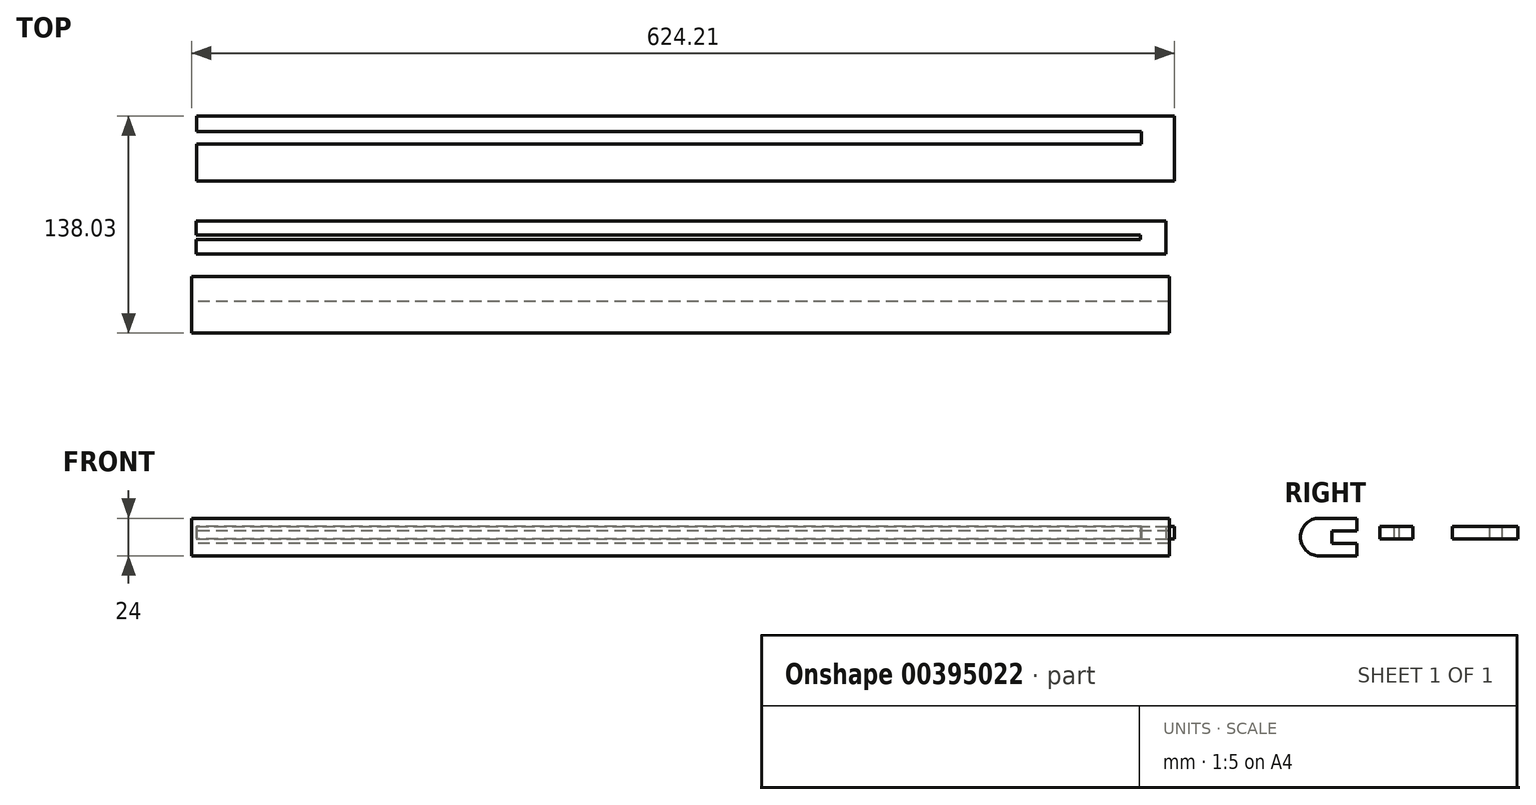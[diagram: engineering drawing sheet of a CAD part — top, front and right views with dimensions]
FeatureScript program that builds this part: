
annotation { "Feature Type Name" : "Feature", "Feature Type Description" : "" }
export const myFeature = defineFeature(function(context is Context, id is Id, definition is map)
    precondition{}
    {
        {
            var Q0;
            Q0=qCreatedBy(makeId("Top.planeOp"),FACE);
            var sketch = newSketch(context, id + "F0", { "sketchPlane" : qUnion([Q0])});
            skLineSegment(sketch, "E0.bottom", {"start": v(-18.34, 16.23) * mm, "end": v(581.66, 16.23) * mm});
            skLineSegment(sketch, "E0.top", {"start": v(-18.34, -4.77) * mm, "end": v(581.66, -4.77) * mm});
            skLineSegment(sketch, "E0.left", {"start": v(-18.34, 16.23) * mm, "end": v(-18.34, -4.77) * mm});
            skLineSegment(sketch, "E1", {"start": v(-18.34, 16.23) * mm, "end": v(-18.34, 7.23) * mm});
            skLineSegment(sketch, "E2", {"start": v(-18.34, -4.77) * mm, "end": v(-18.34, 4.23) * mm});
            skLineSegment(sketch, "E3.bottom", {"start": v(-18.34, 7.23) * mm, "end": v(581.66, 7.23) * mm});
            skLineSegment(sketch, "E3.top", {"start": v(-18.34, 4.23) * mm, "end": v(581.66, 4.23) * mm});
            skLineSegment(sketch, "E3.left", {"start": v(-18.34, 7.23) * mm, "end": v(-18.34, 4.23) * mm});
            skLineSegment(sketch, "E3.right", {"start": v(581.66, 7.23) * mm, "end": v(581.66, 4.23) * mm});
            skLineSegment(sketch, "E4.bottom", {"start": v(581.66, 16.23) * mm, "end": v(597.66, 16.23) * mm});
            skLineSegment(sketch, "E4.top", {"start": v(581.66, -4.77) * mm, "end": v(597.66, -4.77) * mm});
            skLineSegment(sketch, "E4.right", {"start": v(597.66, 16.23) * mm, "end": v(597.66, -4.77) * mm});
            skLineSegment(sketch, "E5", {"start": v(597.66, -4.77) * mm, "end": v(581.66, -4.77) * mm});
            skSolve(sketch);
        }
        {
            var Q0;
            Q0=qCreatedBy(makeId("Top.planeOp"),FACE);
            var sketch = newSketch(context, id + "F1", { "sketchPlane" : qUnion([Q0])});
            skLineSegment(sketch, "E6", {"start": v(-17.8, 41.34) * mm, "end": v(582.2, 41.34) * mm});
            skLineSegment(sketch, "E7", {"start": v(582.2, 41.34) * mm, "end": v(603.2, 41.34) * mm});
            skLineSegment(sketch, "E8", {"start": v(-17.8, 41.34) * mm, "end": v(-17.8, 64.84) * mm});
            skLineSegment(sketch, "E9", {"start": v(-17.8, 64.84) * mm, "end": v(582.2, 64.84) * mm});
            skLineSegment(sketch, "E10", {"start": v(582.2, 64.84) * mm, "end": v(582.2, 72.84) * mm});
            skLineSegment(sketch, "E11", {"start": v(582.2, 72.84) * mm, "end": v(-17.8, 72.84) * mm});
            skLineSegment(sketch, "E12", {"start": v(-17.8, 72.84) * mm, "end": v(-17.8, 82.84) * mm});
            skLineSegment(sketch, "E13", {"start": v(-17.8, 82.84) * mm, "end": v(582.2, 82.84) * mm});
            skLineSegment(sketch, "E14", {"start": v(582.2, 82.84) * mm, "end": v(603.2, 82.84) * mm});
            skLineSegment(sketch, "E15", {"start": v(603.2, 82.84) * mm, "end": v(603.2, 41.34) * mm});
            skSolve(sketch);
        }
        {
            var Q0;
            Q0=makeQuery(id+"F0.imprint","IMPRINT",FACE,{"disambiguationData":[TD([[makeQuery(id+"F0.imprint","IMPRINT",EDGE,{"derivedFrom":sQuery(id+"F0.wireOp",EDGE,"E0.bottom")}),-1.0]])]});
            extrude(context, id + "F2", {"entities" : qUnion([Q0]), "depth" : 8 * mm});
        }
        {
            var Q0;
            Q0=makeQuery(id+"F1.imprint","IMPRINT",FACE,{"disambiguationData":[TD([[makeQuery(id+"F1.imprint","IMPRINT",EDGE,{"derivedFrom":sQuery(id+"F1.wireOp",EDGE,"E6")}),1.0]])]});
            extrude(context, id + "F3", {"entities" : qUnion([Q0]), "depth" : 8 * mm});
        }
        {
            var Q0;
            Q0=qCreatedBy(makeId("Right.planeOp"),FACE);
            var sketch = newSketch(context, id + "F4", { "sketchPlane" : qUnion([Q0])});
            skLineSegment(sketch, "E16", {"start": v(-19.2, 13.24) * mm, "end": v(-19.2, 5.24) * mm});
            skLineSegment(sketch, "E17", {"start": v(-19.2, 5.24) * mm, "end": v(-35.2, 5.24) * mm});
            skLineSegment(sketch, "E18", {"start": v(-35.2, 5.24) * mm, "end": v(-35.2, -2.76) * mm});
            skLineSegment(sketch, "E19", {"start": v(-35.2, -2.76) * mm, "end": v(-19.2, -2.76) * mm});
            skLineSegment(sketch, "E20", {"start": v(-19.2, -2.76) * mm, "end": v(-19.2, -10.76) * mm});
            skLineSegment(sketch, "E21", {"start": v(-19.2, 13.24) * mm, "end": v(-43.2, 13.24) * mm});
            skLineSegment(sketch, "E22", {"start": v(-19.2, -10.76) * mm, "end": v(-43.2, -10.76) * mm});
            skArc(sketch, "E23", {"start": v(-43.2, 13.24) * mm, "mid": v(-55.2, 1.24) * mm, "end": v(-43.2, -10.76) * mm});
            skSolve(sketch);
        }
        {
            var Q0;
            Q0=makeQuery(id+"F4.imprint","IMPRINT",FACE,{"disambiguationData":[TD([[makeQuery(id+"F4.imprint","IMPRINT",EDGE,{"derivedFrom":sQuery(id+"F4.wireOp",EDGE,"E16")}),-1.0]])]});
            extrude(context, id + "F5", {"entities" : qUnion([Q0]), "depth" : 600 * mm});
        }
        {
            var Q0;
            Q0=makeQuery(id+"F5.opExtrude","CAP_FACE",FACE,{"disambiguationData":[OSD([sQuery(id+"F4.wireOp",EDGE,"E16"),sQuery(id+"F4.wireOp",EDGE,"E17"),sQuery(id+"F4.wireOp",EDGE,"E18"),sQuery(id+"F4.wireOp",EDGE,"E19"),sQuery(id+"F4.wireOp",EDGE,"E20"),sQuery(id+"F4.wireOp",EDGE,"E21"),sQuery(id+"F4.wireOp",EDGE,"E22"),sQuery(id+"F4.wireOp",EDGE,"E23")])],"isStart":true});
            extrude(context, id + "F6", {"entities" : qUnion([Q0]), "operationType" : NewBodyOperationType.ADD, "depth" : 21 * mm});
        }
    });
